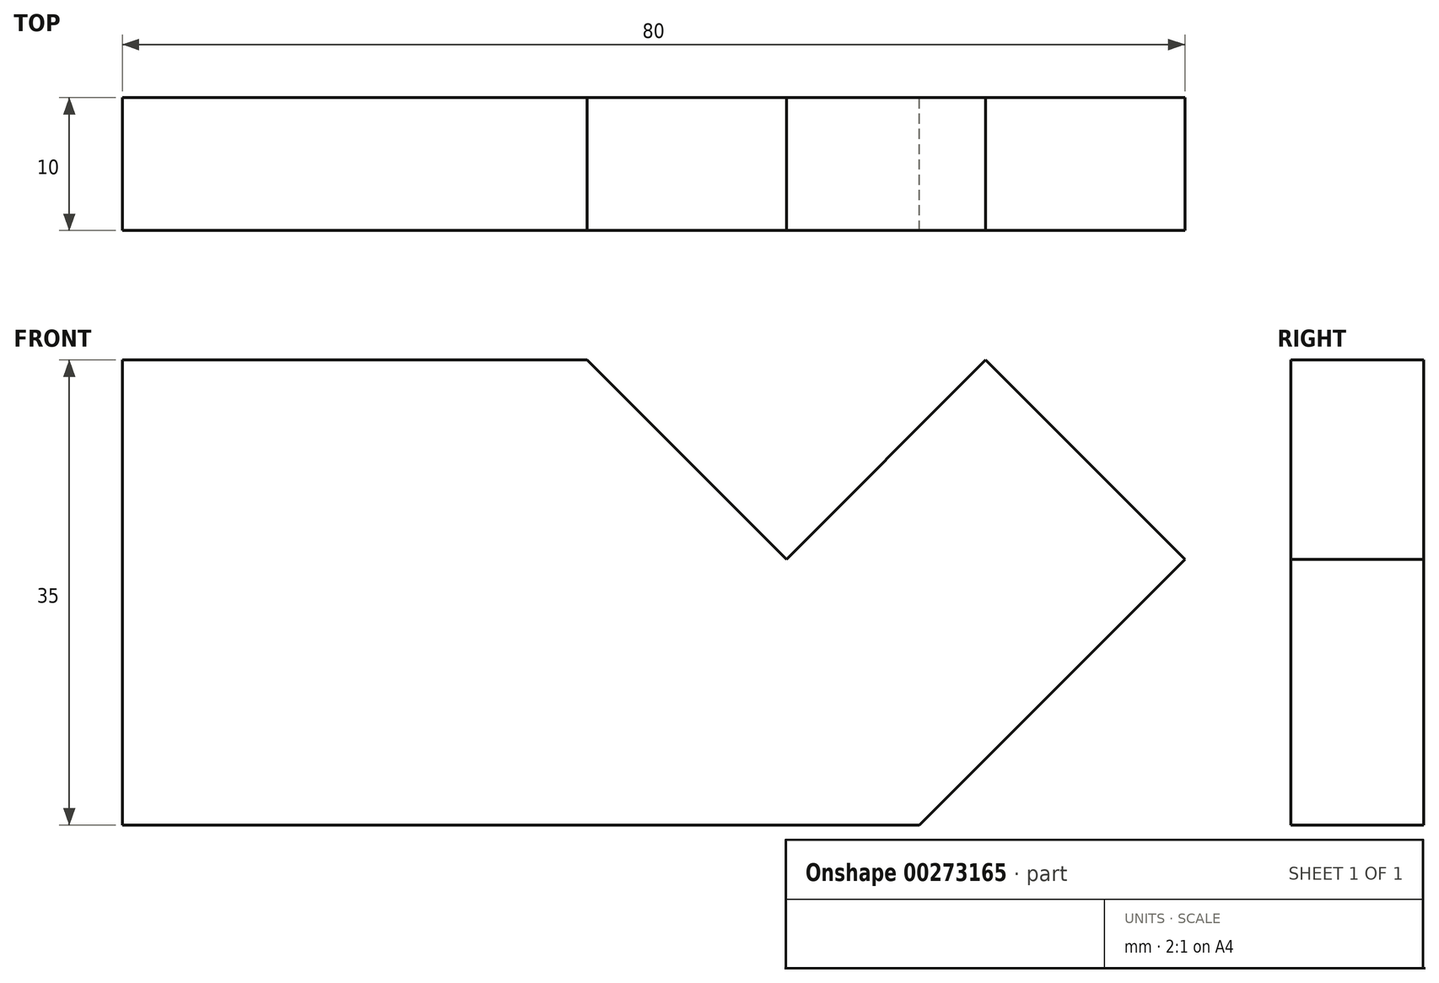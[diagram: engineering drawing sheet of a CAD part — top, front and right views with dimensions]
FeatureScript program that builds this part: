
annotation { "Feature Type Name" : "Feature", "Feature Type Description" : "" }
export const myFeature = defineFeature(function(context is Context, id is Id, definition is map)
    precondition{}
    {
        {
            var Q0;
            Q0=qCreatedBy(makeId("Front.planeOp"),FACE);
            var sketch = newSketch(context, id + "F0", { "sketchPlane" : qUnion([Q0])});
            skLineSegment(sketch, "E0", {"start": v(0, 0) * mm, "end": v(0, 35) * mm});
            skLineSegment(sketch, "E1", {"start": v(0, 35) * mm, "end": v(35, 35) * mm});
            skLineSegment(sketch, "E2", {"start": v(35, 35) * mm, "end": v(50, 20) * mm});
            skLineSegment(sketch, "E3", {"start": v(50, 20) * mm, "end": v(65, 35) * mm});
            skLineSegment(sketch, "E4", {"start": v(65, 35) * mm, "end": v(80, 20) * mm});
            skLineSegment(sketch, "E5", {"start": v(80, 20) * mm, "end": v(60, 0) * mm});
            skLineSegment(sketch, "E6", {"start": v(60, 0) * mm, "end": v(0, 0) * mm});
            skLineSegment(sketch, "E7", {"start": v(50, 47.19) * mm, "end": v(50, -10.4) * mm, "construction": true});
            skSolve(sketch);
        }
        {
            var Q0;
            Q0 = qSketchRegion(id + "F0", true);
            extrude(context, id + "F1", {"entities" : qUnion([Q0]), "depth" : 10 * mm});
        }
    });
